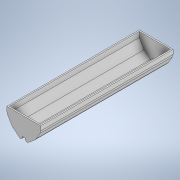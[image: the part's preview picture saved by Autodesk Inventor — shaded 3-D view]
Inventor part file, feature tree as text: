
AUTODESK INVENTOR PART (.ipt)
format: ipt  version: 2020.3 (Build 243373000, 373)  size: 134,656 bytes
history: native  units: mm
features: extrude x1, shell x1, chamfer x1, sketch x1
ambient origin geometry x8: Origin, YZ Plane, XZ Plane, XY Plane, X Axis, Y Axis, Z Axis, Center Point
bodies: Solid1 (feature_tree)
feature tree (4):
  extrude  "Extrusion1"  Depth=2.0mm
  shell  "Shell1"  Thickness=1.0mm
  chamfer  "Chamfer1"  Distance=27.925268mm
  sketch  "Sketch1"  dims[d0=2.0mm d1=2.0mm d2=1.0mm d3=27.925268mm d4=150.0deg d5=100.0mm d6=0.0mm d7=1.0mm d8=1.0mm d9=2.0mm d10=45.0deg]
